FCSTD DOCUMENT  (FreeCAD 0.20R29177 +426 (Git))
Label: ASM_RotationDriver
License: All rights reserved
LicenseURL: http://en.wikipedia.org/wiki/All_rights_reserved
objects: App::Link×8, App::DocumentObjectGroup×3, PartDesign::CoordinateSystem×1, App::FeaturePython×1, App::Part×1
note: 1 computed .brp shape members not serialized (recipe doc carries the construction recipe); baked Part::Feature solids carry a one-line shape summary decoded from their .brp
EXTERNAL_REF file=SerpentinePlate.FCStd obj=LCS_Origin
EXTERNAL_REF file=Stepper17BracketFlat.FCStd obj=LCS_Origin
EXTERNAL_REF file=Stepper17BracketFlat.FCStd obj=Pad
EXTERNAL_REF file=SerpentinePlate.FCStd obj=Assembly
EXTERNAL_REF file=TimingPulleyGT2.FCStd obj=LCS_Origin
EXTERNAL_REF file=TimingPulleyGT2.FCStd obj=Assembly
EXTERNAL_REF file=SerpentinePlate.FCStd obj=LCS_idler1
EXTERNAL_REF file=SmoothIdlerPulleyGT2.FCStd obj=LCS_Origin
EXTERNAL_REF file=SmoothIdlerPulleyGT2.FCStd obj=Assembly
EXTERNAL_REF file=SerpentinePlate.FCStd obj=LCS_idler2
EXTERNAL_REF file=Stepper17BracketFlat.FCStd obj=Assembly
EXTERNAL_REF file=Stepper17.FCStd obj=LCS_mount
EXTERNAL_REF file=Stepper17.FCStd obj=Body
EXTERNAL_REF file=RotationDriverMountingSpacer.FCStd obj=LCS_Origin
EXTERNAL_REF file=Stepper17BracketFlat.FCStd obj=LCS_Mount
EXTERNAL_REF file=RotationDriverMountingSpacer.FCStd obj=Assembly
EXTERNAL_REF file=RotationDriveBelt.FCStd obj=LCS_Origin
EXTERNAL_REF file=RotationDriveBelt.FCStd obj=Assembly

FEATURE [App::DocumentObjectGroup] Parts
FEATURE [PartDesign::CoordinateSystem] LCS_Origin
  AttacherType = Attacher::AttachEngine3D
  MapMode = 2
  Support = -> [X_Axis]
FEATURE [App::FeaturePython] Variables  # WARN: FeaturePython — macro-defined, semantics opaque (R4)
  Type = App::PropertyContainer
FEATURE [App::DocumentObjectGroup] Constraints
FEATURE [App::DocumentObjectGroup] Configurations
FEATURE [App::Link] SerpentinePlate
  AttachedBy = #LCS_Origin
  AttachedTo = Stepper17BracketFlat#LCS_Origin
  AttachmentOffset = pos=(0,0,3) rot=(0,0,1;3.14159rad)
  LinkPlacement = pos=(3e-16,3,0) rot=(1,0,0;4.71239rad)
  LinkedObject = -> <external SerpentinePlate.FCStd>#Assembly
  Placement = pos=(3e-16,3,0) rot=(1,0,0;4.71239rad)
  SolverId = Asm4EE
  expr: .AttachmentOffset.Base.z = <<Stepper17BracketFlat>>#<<Pad>>.Length
  expr: Placement = Stepper17BracketFlat.Placement * Stepper17BracketFlat#LCS_Origin.Placement * AttachmentOffset * SerpentinePlate#LCS_Origin.Placement ^ -1
FEATURE [App::Link] TimingPulleyGT2
  AttachedBy = #LCS_Origin
  AttachedTo = SerpentinePlate#LCS_Origin
  AttachmentOffset = pos=(0,0,23) rot=(0,1,0;3.14159rad)
  LinkPlacement = pos=(2.3e-15,26,0) rot=(0,-0.707107,0.707107;3.14159rad)
  LinkedObject = -> <external TimingPulleyGT2.FCStd>#Assembly
  Placement = pos=(2.3e-15,26,0) rot=(0,-0.707107,0.707107;3.14159rad)
  SolverId = Asm4EE
  expr: Placement = SerpentinePlate.Placement * SerpentinePlate#LCS_Origin.Placement * AttachmentOffset * TimingPulleyGT2#LCS_Origin.Placement ^ -1
FEATURE [App::Link] SmoothIdlerPulleyGT2
  AttachedBy = #LCS_Origin
  AttachedTo = SerpentinePlate#LCS_idler1
  AttachmentOffset = pos=(0,0,1) rot=(0,0,1;0rad)
  LinkPlacement = pos=(16.3,11,7.5) rot=(1,0,0;4.71239rad)
  LinkedObject = -> <external SmoothIdlerPulleyGT2.FCStd>#Assembly
  Placement = pos=(16.3,11,7.5) rot=(1,0,0;4.71239rad)
  SolverId = Asm4EE
  expr: Placement = SerpentinePlate.Placement * SerpentinePlate#LCS_idler1.Placement * AttachmentOffset * SmoothIdlerPulleyGT2#LCS_Origin.Placement ^ -1
FEATURE [App::Link] SmoothIdlerPulleyGT003
  AttachedBy = #LCS_Origin
  AttachedTo = SerpentinePlate#LCS_idler2
  AttachmentOffset = pos=(0,0,1) rot=(0,0,1;0rad)
  LinkPlacement = pos=(-16.3,11,7.5) rot=(1,0,0;4.71239rad)
  LinkedObject = -> <external SmoothIdlerPulleyGT2.FCStd>#Assembly
  Placement = pos=(-16.3,11,7.5) rot=(1,0,0;4.71239rad)
  SolverId = Asm4EE
  expr: Placement = SerpentinePlate.Placement * SerpentinePlate#LCS_idler2.Placement * AttachmentOffset * SmoothIdlerPulleyGT2#LCS_Origin.Placement ^ -1
FEATURE [App::Link] Stepper17BracketFlat
  AttachedBy = #LCS_Origin
  AttachedTo = Parent Assembly#LCS_Origin
  AttachmentOffset = pos=(0,0,0) rot=(0,0.707107,0.707107;3.14159rad)
  LinkPlacement = pos=(0,0,0) rot=(0,0.707107,0.707107;3.14159rad)
  LinkedObject = -> <external Stepper17BracketFlat.FCStd>#Assembly
  Placement = pos=(0,0,0) rot=(0,0.707107,0.707107;3.14159rad)
  SolverId = Asm4EE
  expr: Placement = LCS_Origin.Placement * AttachmentOffset * Stepper17BracketFlat#LCS_Origin.Placement ^ -1
FEATURE [App::Link] Stepper
  AssemblyType = Part::Link
  AttachedBy = #LCS_mount
  AttachedTo = Stepper17BracketFlat#LCS_Origin
  AttachmentOffset = pos=(0,0,0) rot=(0,1,0;3.14159rad)
  LinkPlacement = pos=(0,0,0) rot=(-1,0,0;4.71239rad)
  LinkedObject = -> <external Stepper17.FCStd>#Body
  Placement = pos=(0,0,0) rot=(-1,0,0;4.71239rad)
  SolverId = Asm4EE
  expr: Placement = Stepper17BracketFlat.Placement * Stepper17BracketFlat#LCS_Origin.Placement * AttachmentOffset * Stepper17#LCS_mount.Placement ^ -1
FEATURE [App::Link] RotationDriverMountingSpacer
  AttachedBy = #LCS_Origin
  AttachedTo = Stepper17BracketFlat#LCS_Mount
  AttachmentOffset = pos=(0,0,0) rot=(1,0,0;3.14159rad)
  LinkPlacement = pos=(4.7e-15,0,-53.75) rot=(0,0.707107,-0.707107;3.14159rad)
  LinkedObject = -> <external RotationDriverMountingSpacer.FCStd>#Assembly
  Placement = pos=(4.7e-15,0,-53.75) rot=(0,0.707107,-0.707107;3.14159rad)
  SolverId = Asm4EE
  expr: Placement = Stepper17BracketFlat.Placement * Stepper17BracketFlat#LCS_Mount.Placement * AttachmentOffset * RotationDriverMountingSpacer#LCS_Origin.Placement ^ -1
FEATURE [App::Link] RotationDriveBelt
  AttachedBy = #LCS_Origin
  AttachedTo = TimingPulleyGT2#LCS_Origin
  AttachmentOffset = pos=(0,0,7.7) rot=(0,0,1;3.14159rad)
  LinkPlacement = pos=(2.5e-15,18.3,0) rot=(-1,0,0;4.71239rad)
  LinkedObject = -> <external RotationDriveBelt.FCStd>#Assembly
  Placement = pos=(2.5e-15,18.3,0) rot=(-1,0,0;4.71239rad)
  SolverId = Asm4EE
  expr: Placement = TimingPulleyGT2.Placement * TimingPulleyGT2#LCS_Origin.Placement * AttachmentOffset * RotationDriveBelt#LCS_Origin.Placement ^ -1
FEATURE [App::Part] Assembly
  AssemblyType = Part::Link
  Group = -> [LCS_Origin,Variables,Constraints,Configurations,SerpentinePlate,TimingPulleyGT2,SmoothIdlerPulleyGT2,SmoothIdlerPulleyGT003,Stepper17BracketFlat,Stepper,RotationDriverMountingSpacer,RotationDriveBelt]
  Origin = -> Origin
  Type = Assembly

RESOLVED EXTERNAL PARTS (link-assembly join: the EXTERNAL_REF files above that resolve inside this repo's crawl, each included once):
---- part RotationDriveBelt.FCStd = doc fcstd_e2a3f7d8f1d9 ----
FCSTD DOCUMENT  (FreeCAD 0.20R29177 +426 (Git))
Label: RotationDriveBelt
License: All rights reserved
LicenseURL: http://en.wikipedia.org/wiki/All_rights_reserved
objects: App::DocumentObjectGroup×3, Sketcher::SketchObject×2, PartDesign::Pad×2, PartDesign::Body×2, PartDesign::CoordinateSystem×1, App::FeaturePython×1, App::Part×1
note: 9 computed .brp shape members not serialized (recipe doc carries the construction recipe); baked Part::Feature solids carry a one-line shape summary decoded from their .brp
EXTERNAL_REF file=Params.FCStd obj=Spreadsheet
EXTERNAL_REF file=SerpentinePlate.FCStd obj=Variables

FEATURE [App::DocumentObjectGroup] Parts
FEATURE [PartDesign::CoordinateSystem] LCS_Origin
  AttacherType = Attacher::AttachEngine3D
  MapMode = 2
  Support = -> [X_Axis]
FEATURE [App::FeaturePython] Variables  # WARN: FeaturePython — macro-defined, semantics opaque (R4)
  Type = App::PropertyContainer
FEATURE [App::DocumentObjectGroup] Constraints
FEATURE [App::DocumentObjectGroup] Configurations
FEATURE [Sketcher::SketchObject] Sketch
  FullyConstrained = true
  MapMode = 5
  Support = -> [XY_Plane001]
  expr: Constraints[0] = <<SerpentinePlate>>#<<Variables>>.IdlerMountOffsetX
  expr: Constraints[10] = <<Params>>#<<Params>>.CeilingPlateDiameter / 2 + <<Params>>#<<Params>>.RotationDriveOffset
  expr: Constraints[11] = <<SerpentinePlate>>#<<Variables>>.IdlerMountOffsetY
  expr: Constraints[3] = <<Params>>#<<Params>>.CeilingPlateDiameter + 1
  sketch-geometry (9):
    g0: ArcOfCircle CenterX=1.16e-14 CenterY=-260.5 CenterZ=0 NormalX=0 NormalY=0 NormalZ=1 AngleXU=0 Radius=232 StartAngle=2.20872 EndAngle=7.21605
    g1: ArcOfCircle CenterX=16.3 CenterY=7.5 CenterZ=0 NormalX=0 NormalY=0 NormalZ=1 AngleXU=0 Radius=7 StartAngle=0.932868 EndAngle=2.93081
    g2: ArcOfCircle CenterX=0 CenterY=0 CenterZ=0 NormalX=0 NormalY=0 NormalZ=1 AngleXU=0 Radius=7.37 StartAngle=3.35238 EndAngle=6.0724
    g3: ArcOfCircle CenterX=1.16e-14 CenterY=-260.5 CenterZ=0 NormalX=0 NormalY=0 NormalZ=1 AngleXU=0 Radius=232 StartAngle=0.932868 EndAngle=1.5708
    g4: ArcOfCircle CenterX=-16.3 CenterY=7.5 CenterZ=0 NormalX=0 NormalY=0 NormalZ=1 AngleXU=0 Radius=7 StartAngle=0.210787 EndAngle=2.20872
    g5: LineSegment StartX=7.20688 StartY=-1.54202 StartZ=0 EndX=9.45493 EndY=8.96461 EndZ=0
    g6: LineSegment StartX=138.163 StartY=-74.1271 StartZ=0 EndX=20.4687 EndY=13.1233 EndZ=0
    g7: LineSegment StartX=-7.20688 StartY=-1.54202 StartZ=0 EndX=-9.45493 EndY=8.96461 EndZ=0
    g8: LineSegment StartX=-138.163 StartY=-74.1271 StartZ=0 EndX=-20.4687 EndY=13.1233 EndZ=0
  constraints (22):
    c: DistanceX(g2,g1) = 16.3
    c: Radius(g1) = 7
    c: Radius(g2) = 7.37
    c: Diameter(g0) = 464
    c: PointOnObject(g3,g-2)
    c: Tangent(g3,g0) = -1.5708
    c: Coincident(g3,g0)
    c: Coincident(g2,g-1)
    c: PointOnObject(g0,g-2)
    c: Equal(g4,g1)
    c: DistanceY(g0,g2) = 260.5
    c: DistanceY(g2,g1) = 7.5
    c: Tangent(g5,g1) = 1.5708
    c: Tangent(g5,g2) = -1.5708
    c: Tangent(g6,g1) = -1.5708
    c: Tangent(g6,g0) = -1.5708
    c: Tangent(g7,g4) = -1.5708
    c: Tangent(g7,g2) = 1.5708
    c: Tangent(g8,g4) = 1.5708
    c: Tangent(g8,g0) = 1.5708
    c: Equal(g7,g5)
    c: Equal(g6,g8)
FEATURE [PartDesign::Pad] Pad
  Direction = (0,0,1)
  Length = 6
  Length2 = 10
  Profile = -> Sketch
  ReferenceAxis = -> Sketch [N_Axis]
  Type = 0
FEATURE [PartDesign::Body] Body  label="PerimeterCalc"
  Group = -> [Sketch,Pad]
  Origin = -> Origin001
  Tip = -> Pad
FEATURE [Sketcher::SketchObject] Sketch001
  FullyConstrained = true
  MapMode = 5
  Support = -> [XY_Plane002]
  expr: Constraints[0] = <<SerpentinePlate>>#<<Variables>>.IdlerMountOffsetX
  expr: Constraints[10] = <<Params>>#<<Params>>.CeilingPlateDiameter / 2 + <<Params>>#<<Params>>.RotationDriveOffset
  expr: Constraints[11] = <<SerpentinePlate>>#<<Variables>>.IdlerMountOffsetY
  expr: Constraints[3] = <<Params>>#<<Params>>.CeilingPlateDiameter + 1
  sketch-geometry (19):
    g0: ArcOfCircle CenterX=0 CenterY=-260.5 CenterZ=0 NormalX=0 NormalY=0 NormalZ=1 AngleXU=0 Radius=232 StartAngle=2.20872 EndAngle=7.21605
    g1: ArcOfCircle CenterX=16.3 CenterY=7.5 CenterZ=0 NormalX=0 NormalY=0 NormalZ=1 AngleXU=0 Radius=7 StartAngle=0.932868 EndAngle=2.93081
    g2: ArcOfCircle CenterX=0 CenterY=0 CenterZ=0 NormalX=0 NormalY=0 NormalZ=1 AngleXU=0 Radius=7.37 StartAngle=3.35238 EndAngle=6.0724
    g3: ArcOfCircle CenterX=0 CenterY=-260.5 CenterZ=0 NormalX=0 NormalY=0 NormalZ=1 AngleXU=0 Radius=232 StartAngle=0.932868 EndAngle=1.5708
    g4: ArcOfCircle CenterX=-16.3 CenterY=7.5 CenterZ=0 NormalX=0 NormalY=0 NormalZ=1 AngleXU=0 Radius=7 StartAngle=0.210787 EndAngle=2.20872
    g5: LineSegment StartX=7.20688 StartY=-1.54202 StartZ=0 EndX=9.45493 EndY=8.96461 EndZ=0
    g6: LineSegment StartX=138.163 StartY=-74.1271 StartZ=0 EndX=20.4687 EndY=13.1233 EndZ=0
    g7: LineSegment StartX=-7.20688 StartY=-1.54202 StartZ=0 EndX=-9.45493 EndY=8.96461 EndZ=0
    g8: LineSegment StartX=-138.163 StartY=-74.1271 StartZ=0 EndX=-20.4687 EndY=13.1233 EndZ=0
    g9: ArcOfCircle CenterX=0 CenterY=-260.5 CenterZ=0 NormalX=0 NormalY=0 NormalZ=1 AngleXU=0 Radius=230 StartAngle=2.20872 EndAngle=7.21605
    g10: ArcOfCircle CenterX=16.3 CenterY=7.5 CenterZ=0 NormalX=0 NormalY=0 NormalZ=1 AngleXU=0 Radius=5 StartAngle=0.932868 EndAngle=2.93081
    g11: ArcOfCircle CenterX=0 CenterY=0 CenterZ=0 NormalX=0 NormalY=0 NormalZ=1 AngleXU=0 Radius=9.37 StartAngle=3.35238 EndAngle=6.0724
    g12: ArcOfCircle CenterX=-16.3 CenterY=7.5 CenterZ=0 NormalX=0 NormalY=0 NormalZ=1 AngleXU=0 Radius=5 StartAngle=0.210787 EndAngle=2.20872
    g13: LineSegment StartX=9.16261 StartY=-1.96048 StartZ=0 EndX=11.4107 EndY=8.54615 EndZ=0
    g14: LineSegment StartX=136.972 StartY=-75.7338 StartZ=0 EndX=19.2777 EndY=11.5167 EndZ=0
    g15: LineSegment StartX=-9.16261 StartY=-1.96048 StartZ=0 EndX=-11.4107 EndY=8.54615 EndZ=0
    g16: LineSegment StartX=-136.972 StartY=-75.7338 StartZ=0 EndX=-19.2777 EndY=11.5167 EndZ=0
    g17: LineSegment StartX=11.4107 StartY=8.54615 StartZ=0 EndX=9.45493 EndY=8.96461 EndZ=0
    g18: LineSegment StartX=138.163 StartY=-74.1271 StartZ=0 EndX=136.972 EndY=-75.7338 EndZ=0
  constraints (45):
    c: DistanceX(g2,g1) = 16.3
    c: Radius(g1) = 7
    c: Radius(g2) = 7.37
    c: Diameter(g0) = 464
    c: PointOnObject(g3,g-2)
    c: Tangent(g3,g0) = -1.5708
    c: Coincident(g3,g0)
    c: Coincident(g2,g-1)
    c: PointOnObject(g0,g-2)
    c: Equal(g4,g1)
    c: DistanceY(g0,g2) = 260.5
    c: DistanceY(g2,g1) = 7.5
    c: Tangent(g5,g1) = 1.5708
    c: Tangent(g5,g2) = -1.5708
    c: Tangent(g6,g1) = -1.5708
    c: Tangent(g6,g0) = -1.5708
    c: Tangent(g7,g4) = -1.5708
    c: Tangent(g7,g2) = 1.5708
    c: Tangent(g8,g4) = 1.5708
    c: Tangent(g8,g0) = 1.5708
    c: Equal(g7,g5)
    c: Equal(g6,g8)
    c: DistanceX(g11,g10) = 16.3
    c: DistanceY(g11,g10) = 7.5
    c: Tangent(g13,g10) = 1.5708
    c: Tangent(g13,g11) = -1.5708
    c: Tangent(g14,g10) = -1.5708
    c: Tangent(g14,g9) = -1.5708
    c: Tangent(g15,g12) = -1.5708
    c: Tangent(g15,g11) = 1.5708
    c: Tangent(g16,g12) = 1.5708
    c: Tangent(g16,g9) = 1.5708
    c: Equal(g15,g13)
    c: Coincident(g9,g0)
    c: Coincident(g11,g2)
    c: Coincident(g12,g4)
    c: Coincident(g17,g10)
    c: Perpendicular(g13,g17)
    c: PointOnObject(g17,g5)
    c: Parallel(g13,g5)
    c: Distance(g17) = 2
    c: Coincident(g18,g0)
    c: Perpendicular(g6,g18)
    c: PointOnObject(g18,g14)
    c: Equal(g18,g17)
FEATURE [PartDesign::Pad] Pad001
  Direction = (0,0,1)
  Length = 6
  Length2 = 10
  Profile = -> Sketch001
  ReferenceAxis = -> Sketch001 [N_Axis]
  Type = 0
FEATURE [PartDesign::Body] Body001
  Group = -> [Sketch001,Pad001]
  Origin = -> Origin002
  Tip = -> Pad001
FEATURE [App::Part] Assembly
  AssemblyType = Part::Link
  Group = -> [LCS_Origin,Variables,Constraints,Configurations,Body,Body001]
  Origin = -> Origin
  Type = Assembly
---- part RotationDriverMountingSpacer.FCStd = doc fcstd_c8136d02d082 ----
FCSTD DOCUMENT  (FreeCAD 0.20R29177 +426 (Git))
Label: RotationDriverMountingSpacer
License: All rights reserved
LicenseURL: http://en.wikipedia.org/wiki/All_rights_reserved
objects: Part::FeaturePython×16, App::DocumentObjectGroup×8, Sketcher::SketchObject×2, PartDesign::CoordinateSystem×1, App::FeaturePython×1, PartDesign::Pad×1, PartDesign::Hole×1, PartDesign::Body×1, App::Part×1
note: 24 computed .brp shape members not serialized (recipe doc carries the construction recipe); baked Part::Feature solids carry a one-line shape summary decoded from their .brp
EXTERNAL_REF file=Params.FCStd obj=Spreadsheet
EXTERNAL_REF file=Stepper17BracketFlat.FCStd obj=Pad

FEATURE [App::DocumentObjectGroup] Parts
FEATURE [PartDesign::CoordinateSystem] LCS_Origin
  AttacherType = Attacher::AttachEngine3D
  MapMode = 2
  Support = -> [X_Axis]
FEATURE [App::FeaturePython] Variables  # WARN: FeaturePython — macro-defined, semantics opaque (R4)
  BracketHoleSpacing = 30
  Type = App::PropertyContainer
FEATURE [App::DocumentObjectGroup] Constraints
FEATURE [App::DocumentObjectGroup] Configurations
FEATURE [Sketcher::SketchObject] Sketch
  FullyConstrained = true
  MapMode = 5
  Support = -> [XY_Plane001]
  expr: Constraints[26] = <<Variables>>.BracketHoleSpacing
  sketch-geometry (24):
    g0: LineSegment StartX=-15 StartY=-15 StartZ=0 EndX=-15 EndY=15 EndZ=0
    g1: LineSegment StartX=-15 StartY=15 StartZ=0 EndX=15 EndY=15 EndZ=0
    g2: LineSegment StartX=15 StartY=15 StartZ=0 EndX=15 EndY=-15 EndZ=0
    g3: LineSegment StartX=15 StartY=-15 StartZ=0 EndX=-15 EndY=-15 EndZ=0
    g4: GeomPoint X=0 Y=0 Z=0
    g5: ArcOfCircle CenterX=15 CenterY=15 CenterZ=0 NormalX=0 NormalY=0 NormalZ=1 AngleXU=0 Radius=2.15 StartAngle=0 EndAngle=3.14159
    g6: ArcOfCircle CenterX=15 CenterY=-15 CenterZ=0 NormalX=0 NormalY=0 NormalZ=1 AngleXU=0 Radius=2.15 StartAngle=3.14159 EndAngle=6.28319
    g7: LineSegment StartX=12.85 StartY=15 StartZ=0 EndX=12.85 EndY=-15 EndZ=0
    g8: LineSegment StartX=17.15 StartY=-15 StartZ=0 EndX=17.15 EndY=15 EndZ=0
    g9: ArcOfCircle CenterX=-15 CenterY=15 CenterZ=0 NormalX=0 NormalY=0 NormalZ=1 AngleXU=0 Radius=2.15 StartAngle=0 EndAngle=3.14159
    g10: ArcOfCircle CenterX=-15 CenterY=-15 CenterZ=0 NormalX=0 NormalY=0 NormalZ=1 AngleXU=0 Radius=2.15 StartAngle=3.14159 EndAngle=6.28319
    g11: LineSegment StartX=-17.15 StartY=15 StartZ=0 EndX=-17.15 EndY=-15 EndZ=0
    g12: LineSegment StartX=-12.85 StartY=-15 StartZ=0 EndX=-12.85 EndY=15 EndZ=0
    g13: ArcOfCircle CenterX=-15 CenterY=15 CenterZ=0 NormalX=0 NormalY=0 NormalZ=1 AngleXU=0 Radius=10 StartAngle=1.5708 EndAngle=3.14159
    g14: LineSegment StartX=-15 StartY=25 StartZ=0 EndX=15 EndY=25 EndZ=0
    g15: ArcOfCircle CenterX=15 CenterY=15 CenterZ=0 NormalX=0 NormalY=0 NormalZ=1 AngleXU=0 Radius=10 StartAngle=1e-16 EndAngle=1.5708
    g16: LineSegment StartX=25 StartY=15 StartZ=0 EndX=25 EndY=-15 EndZ=0
    g17: ArcOfCircle CenterX=15 CenterY=-15 CenterZ=0 NormalX=0 NormalY=0 NormalZ=1 AngleXU=0 Radius=10 StartAngle=4.71239 EndAngle=6.28319
    g18: LineSegment StartX=15 StartY=-25 StartZ=0 EndX=-15 EndY=-25 EndZ=0
    g19: ArcOfCircle CenterX=-15 CenterY=-15 CenterZ=0 NormalX=0 NormalY=0 NormalZ=1 AngleXU=0 Radius=10 StartAngle=3.14159 EndAngle=4.71239
    g20: LineSegment StartX=-25 StartY=-15 StartZ=0 EndX=-25 EndY=15 EndZ=0
    g21: GeomPoint X=-25 Y=25 Z=0
    g22: GeomPoint X=25 Y=-25 Z=0
    g23: Circle CenterX=0 CenterY=0 CenterZ=0 NormalX=0 NormalY=0 NormalZ=1 AngleXU=0 Radius=14
  constraints (52):
    c: Coincident(g0,g1)
    c: Coincident(g1,g2)
    c: Coincident(g2,g3)
    c: Coincident(g3,g0)
    c: Horizontal(g1)
    c: Horizontal(g3)
    c: Vertical(g0)
    c: Vertical(g2)
    c: Symmetric(g1,g0,g4)
    c: Coincident(g4,g-1)
    c: Tangent(g5,g7) = -1.5708
    c: Tangent(g7,g6) = -1.5708
    c: Tangent(g6,g8) = -1.5708
    c: Tangent(g8,g5) = -1.5708
    c: Equal(g5,g6)
    c: Coincident(g5,g1)
    c: Coincident(g6,g2)
    c: Tangent(g9,g11) = -1.5708
    c: Tangent(g11,g10) = -1.5708
    c: Tangent(g10,g12) = -1.5708
    c: Tangent(g12,g9) = -1.5708
    c: Equal(g9,g10)
    c: Coincident(g9,g0)
    c: Coincident(g10,g0)
    c: Equal(g5,g9)
    c: Diameter(g5) = 4.3
    c: DistanceX(g1,g1) = 30
    c: Equal(g2,g1)
    c: Tangent(g13,g14) = 1.5708
    c: Tangent(g14,g15) = 1.5708
    c: Tangent(g15,g16) = 1.5708
    c: Tangent(g16,g17) = 1.5708
    c: Tangent(g17,g18) = 1.5708
    c: Tangent(g18,g19) = 1.5708
    c: Tangent(g19,g20) = 1.5708
    c: Tangent(g20,g13) = 1.5708
    c: Horizontal(g14)
    c: Horizontal(g18)
    c: Vertical(g16)
    c: Vertical(g20)
    c: Equal(g13,g15)
    c: Equal(g15,g17)
    c: Equal(g17,g19)
    c: PointOnObject(g21,g14)
    c: PointOnObject(g21,g20)
    c: PointOnObject(g22,g16)
    c: PointOnObject(g22,g18)
    c: Coincident(g13,g9)
    c: Coincident(g17,g6)
    c: DistanceX(g13,g15) = 50
    c: Coincident(g23,g4)
    c: Diameter(g23) = 28
FEATURE [PartDesign::Pad] Pad
  Direction = (0,0,1)
  Length = 9
  Length2 = 10
  Profile = -> Sketch
  ReferenceAxis = -> Sketch [N_Axis]
  Type = 0
FEATURE [Sketcher::SketchObject] Sketch001
  FullyConstrained = true
  MapMode = 5
  Support = -> [XY_Plane001]
  sketch-geometry (9):
    g0: LineSegment StartX=-15 StartY=-15 StartZ=0 EndX=-15 EndY=15 EndZ=0
    g1: LineSegment StartX=-15 StartY=15 StartZ=0 EndX=15 EndY=15 EndZ=0
    g2: LineSegment StartX=15 StartY=15 StartZ=0 EndX=15 EndY=-15 EndZ=0
    g3: LineSegment StartX=15 StartY=-15 StartZ=0 EndX=-15 EndY=-15 EndZ=0
    g4: GeomPoint X=0 Y=0 Z=0
    g5: Circle CenterX=15 CenterY=15 CenterZ=0 NormalX=0 NormalY=0 NormalZ=1 AngleXU=0 Radius=1
    g6: Circle CenterX=15 CenterY=-15 CenterZ=0 NormalX=0 NormalY=0 NormalZ=1 AngleXU=0 Radius=1
    g7: Circle CenterX=-15 CenterY=15 CenterZ=0 NormalX=0 NormalY=0 NormalZ=1 AngleXU=0 Radius=1
    g8: Circle CenterX=-15 CenterY=-15 CenterZ=0 NormalX=0 NormalY=0 NormalZ=1 AngleXU=0 Radius=1
  constraints (20):
    c: Coincident(g0,g1)
    c: Coincident(g1,g2)
    c: Coincident(g2,g3)
    c: Coincident(g3,g0)
    c: Horizontal(g1)
    c: Horizontal(g3)
    c: Vertical(g0)
    c: Vertical(g2)
    c: Symmetric(g1,g0,g4)
    c: Coincident(g4,g-1)
    c: DistanceX(g1,g1) = 30
    c: Equal(g2,g1)
    c: Coincident(g5,g1)
    c: Coincident(g6,g2)
    c: Coincident(g7,g0)
    c: Coincident(g8,g0)
    c: Equal(g8,g6)
    c: Equal(g6,g5)
    c: Equal(g5,g7)
    c: Diameter(g5) = 2
FEATURE [PartDesign::Hole] Hole  label="BracketMountHoles"
  BaseFeature = -> Pad
  CustomThreadClearance = 0
  Depth = 143.988
  DepthType = 1
  Diameter = 4.8
  DrillForDepth = false
  DrillPoint = 1
  DrillPointAngle = 118
  HoleCutCountersinkAngle = 90
  HoleCutCustomValues = false
  HoleCutDepth = 0
  HoleCutDiameter = 6.1
  HoleCutType = 0
  ModelThread = false
  Profile = -> Sketch001
  Reversed = true
  Tapered = false
  TaperedAngle = 90
  ThreadClass = 0
  ThreadDepth = 143.988
  ThreadDepthType = 0
  ThreadDirection = 0
  ThreadFit = 2
  ThreadSize = 0
  ThreadType = 0
  Threaded = false
  UseCustomThreadClearance = false
FEATURE [PartDesign::Body] Body
  Group = -> [Sketch,Pad,Sketch001,Hole]
  Origin = -> Origin001
  Tip = -> Hole
FEATURE [Part::FeaturePython] Washer  label="M4-Washer"  # Fasteners workbench fastener (typed FeaturePython)
  Placement = pos=(15,-15,11.656) rot=(0,0,1;0rad)
  baseObject = -> Sketch001 [Edge2]
  diameter = 5
  invert = false
  matchOuter = true
  offset = 11.656
  type = 3
  expr: offset = <<Pad>>.Length + <<Params>>#<<Params>>.SheetMetalThickness * 1mm
FEATURE [Part::FeaturePython] Screw  label="M4x20-Screw"  # Fasteners workbench fastener (typed FeaturePython)
  Placement = pos=(15,-15,12.456) rot=(0,0,1;0rad)
  baseObject = -> Washer [Edge1]
  diameter = 5
  invert = false
  leftHanded = false
  length = 6
  lengthCustom = 20
  matchOuter = true
  offset = 0
  thread = false
  type = 34
FEATURE [Part::FeaturePython] Washer001  label="M4-Washer022"  # Fasteners workbench fastener (typed FeaturePython)
  Placement = pos=(15,-15,-3) rot=(1,0,0;3.14159rad)
  baseObject = -> Washer [Edge3]
  diameter = 5
  invert = true
  matchOuter = true
  offset = 14.656
  type = 3
  expr: offset = <<Pad>>.Length + <<Params>>#<<Params>>.SheetMetalThickness * 1mm + <<Stepper17BracketFlat>>#<<Pad>>.Length
FEATURE [Part::FeaturePython] Nut  label="M4-Nut"  # Fasteners workbench fastener (typed FeaturePython)
  Placement = pos=(15,-15,-3.8) rot=(1,0,0;3.14159rad)
  baseObject = -> Washer001 [Edge1]
  diameter = 6
  invert = false
  leftHanded = false
  matchOuter = true
  offset = 0
  thread = false
  type = 7
FEATURE [App::DocumentObjectGroup] Hole1
  Group = -> [Screw,Washer,Washer001,Nut]
FEATURE [Part::FeaturePython] Nut001  label="M4-Nut010"  # Fasteners workbench fastener (typed FeaturePython)
  Placement = pos=(-15,-15,-3.8) rot=(1,0,0;3.14159rad)
  baseObject = -> Washer003 [Edge1]
  diameter = 6
  invert = false
  leftHanded = false
  matchOuter = true
  offset = 0
  thread = false
  type = 7
FEATURE [Part::FeaturePython] Screw001  label="M4x20-Screw010"  # Fasteners workbench fastener (typed FeaturePython)
  Placement = pos=(-15,-15,12.456) rot=(0,0,1;0rad)
  baseObject = -> Washer002 [Edge1]
  diameter = 5
  invert = false
  leftHanded = false
  length = 6
  lengthCustom = 20
  matchOuter = true
  offset = 0
  thread = false
  type = 34
FEATURE [Part::FeaturePython] Washer002  label="M4-Washer023"  # Fasteners workbench fastener (typed FeaturePython)
  Placement = pos=(-15,-15,11.656) rot=(0,0,1;0rad)
  baseObject = -> Sketch001 [Edge4]
  diameter = 5
  invert = false
  matchOuter = true
  offset = 11.656
  type = 3
  expr: offset = <<Pad>>.Length + <<Params>>#<<Params>>.SheetMetalThickness * 1mm
FEATURE [Part::FeaturePython] Washer003  label="M4-Washer024"  # Fasteners workbench fastener (typed FeaturePython)
  Placement = pos=(-15,-15,-3) rot=(1,0,0;3.14159rad)
  baseObject = -> Washer002 [Edge3]
  diameter = 5
  invert = true
  matchOuter = true
  offset = 14.656
  type = 3
  expr: offset = <<Pad>>.Length + <<Params>>#<<Params>>.SheetMetalThickness * 1mm + <<Stepper17BracketFlat>>#<<Pad>>.Length
FEATURE [App::DocumentObjectGroup] Hole002
  Group = -> [Screw001,Washer002,Washer003,Nut001]
FEATURE [Part::FeaturePython] Nut002  label="M4-Nut011"  # Fasteners workbench fastener (typed FeaturePython)
  Placement = pos=(-15,15,-3.8) rot=(1,0,0;3.14159rad)
  baseObject = -> Washer005 [Edge1]
  diameter = 6
  invert = false
  leftHanded = false
  matchOuter = true
  offset = 0
  thread = false
  type = 7
FEATURE [Part::FeaturePython] Screw002  label="M4x20-Screw011"  # Fasteners workbench fastener (typed FeaturePython)
  Placement = pos=(-15,15,12.456) rot=(0,0,1;0rad)
  baseObject = -> Washer004 [Edge1]
  diameter = 5
  invert = false
  leftHanded = false
  length = 6
  lengthCustom = 20
  matchOuter = true
  offset = 0
  thread = false
  type = 34
FEATURE [Part::FeaturePython] Washer004  label="M4-Washer025"  # Fasteners workbench fastener (typed FeaturePython)
  Placement = pos=(-15,15,11.656) rot=(0,0,1;0rad)
  baseObject = -> Sketch001 [Edge3]
  diameter = 5
  invert = false
  matchOuter = true
  offset = 11.656
  type = 3
  expr: offset = <<Pad>>.Length + <<Params>>#<<Params>>.SheetMetalThickness * 1mm
FEATURE [Part::FeaturePython] Washer005  label="M4-Washer026"  # Fasteners workbench fastener (typed FeaturePython)
  Placement = pos=(-15,15,-3) rot=(1,0,0;3.14159rad)
  baseObject = -> Washer004 [Edge3]
  diameter = 5
  invert = true
  matchOuter = true
  offset = 14.656
  type = 3
  expr: offset = <<Pad>>.Length + <<Params>>#<<Params>>.SheetMetalThickness * 1mm + <<Stepper17BracketFlat>>#<<Pad>>.Length
FEATURE [App::DocumentObjectGroup] Hole003
  Group = -> [Screw002,Washer004,Washer005,Nut002]
FEATURE [Part::FeaturePython] Nut003  label="M4-Nut012"  # Fasteners workbench fastener (typed FeaturePython)
  Placement = pos=(15,15,-3.8) rot=(1,0,0;3.14159rad)
  baseObject = -> Washer007 [Edge1]
  diameter = 6
  invert = false
  leftHanded = false
  matchOuter = true
  offset = 0
  thread = false
  type = 7
FEATURE [Part::FeaturePython] Screw003  label="M4x20-Screw012"  # Fasteners workbench fastener (typed FeaturePython)
  Placement = pos=(15,15,12.456) rot=(0,0,1;0rad)
  baseObject = -> Washer006 [Edge1]
  diameter = 5
  invert = false
  leftHanded = false
  length = 6
  lengthCustom = 20
  matchOuter = true
  offset = 0
  thread = false
  type = 34
FEATURE [Part::FeaturePython] Washer006  label="M4-Washer027"  # Fasteners workbench fastener (typed FeaturePython)
  Placement = pos=(15,15,11.656) rot=(0,0,1;0rad)
  baseObject = -> Sketch001 [Edge1]
  diameter = 5
  invert = false
  matchOuter = true
  offset = 11.656
  type = 3
  expr: offset = <<Pad>>.Length + <<Params>>#<<Params>>.SheetMetalThickness * 1mm
FEATURE [Part::FeaturePython] Washer007  label="M4-Washer028"  # Fasteners workbench fastener (typed FeaturePython)
  Placement = pos=(15,15,-3) rot=(1,0,0;3.14159rad)
  baseObject = -> Washer006 [Edge3]
  diameter = 5
  invert = true
  matchOuter = true
  offset = 14.656
  type = 3
  expr: offset = <<Pad>>.Length + <<Params>>#<<Params>>.SheetMetalThickness * 1mm + <<Stepper17BracketFlat>>#<<Pad>>.Length
FEATURE [App::DocumentObjectGroup] Hole004
  Group = -> [Screw003,Washer006,Washer007,Nut003]
FEATURE [App::DocumentObjectGroup] Fasteners
  Group = -> [Hole1,Hole002,Hole003,Hole004]
FEATURE [App::Part] Assembly
  AssemblyType = Part::Link
  Group = -> [LCS_Origin,Variables,Constraints,Configurations,Body,Fasteners,Washer,Screw,Washer001,Nut,Hole1,Washer002,Screw001,Washer003,Nut001,Hole002,Washer005,Nut002,Screw002,Washer004,Hole003,Washer007,Screw003,Nut003,Washer006,Hole004]
  Origin = -> Origin
  Type = Assembly
---- part SerpentinePlate.FCStd = doc fcstd_52ecc4b848b1 ----
FCSTD DOCUMENT  (FreeCAD 0.20R29177 +426 (Git))
Label: SerpentinePlate
License: All rights reserved
LicenseURL: http://en.wikipedia.org/wiki/All_rights_reserved
objects: Part::FeaturePython×8, App::DocumentObjectGroup×4, PartDesign::Hole×4, PartDesign::CoordinateSystem×3, Sketcher::SketchObject×3, App::FeaturePython×1, PartDesign::Pad×1, PartDesign::Body×1, App::Part×1
note: 25 computed .brp shape members not serialized (recipe doc carries the construction recipe); baked Part::Feature solids carry a one-line shape summary decoded from their .brp

FEATURE [App::DocumentObjectGroup] Parts
FEATURE [PartDesign::CoordinateSystem] LCS_Origin
  AttacherType = Attacher::AttachEngine3D
  MapMode = 2
  Support = -> [X_Axis]
FEATURE [App::FeaturePython] Variables  # WARN: FeaturePython — macro-defined, semantics opaque (R4)
  IdlerMountOffsetX = 16.3
  IdlerMountOffsetY = 7.5
  Type = App::PropertyContainer
FEATURE [App::DocumentObjectGroup] Constraints
FEATURE [App::DocumentObjectGroup] Configurations
FEATURE [Sketcher::SketchObject] Sketch
  FullyConstrained = true
  MapMode = 5
  Support = -> [XY_Plane001]
  sketch-geometry (23):
    g0: LineSegment StartX=-15.5 StartY=15.5 StartZ=0 EndX=-15.5 EndY=-15.5 EndZ=0
    g1: LineSegment StartX=-15.5 StartY=-15.5 StartZ=0 EndX=15.5 EndY=-15.5 EndZ=0
    g2: LineSegment StartX=15.5 StartY=-15.5 StartZ=0 EndX=15.5 EndY=15.5 EndZ=0
    g3: LineSegment StartX=15.5 StartY=15.5 StartZ=0 EndX=-15.5 EndY=15.5 EndZ=0
    g4: GeomPoint X=0 Y=0 Z=0
    g5: Circle CenterX=-15.5 CenterY=15.5 CenterZ=0 NormalX=0 NormalY=0 NormalZ=1 AngleXU=0 Radius=1.7
    g6: Circle CenterX=15.5 CenterY=15.5 CenterZ=0 NormalX=0 NormalY=0 NormalZ=1 AngleXU=0 Radius=1.7
    g7: Circle CenterX=15.5 CenterY=-15.5 CenterZ=0 NormalX=0 NormalY=0 NormalZ=1 AngleXU=0 Radius=1.7
    g8: Circle CenterX=-15.5 CenterY=-15.5 CenterZ=0 NormalX=0 NormalY=0 NormalZ=1 AngleXU=0 Radius=1.7
    g9: Circle CenterX=0 CenterY=0 CenterZ=0 NormalX=0 NormalY=0 NormalZ=1 AngleXU=0 Radius=11.3
    g10: Circle CenterX=0 CenterY=0 CenterZ=0 NormalX=0 NormalY=0 NormalZ=1 AngleXU=0 Radius=6.11
    g11: ArcOfCircle CenterX=-15.5 CenterY=13 CenterZ=0 NormalX=0 NormalY=0 NormalZ=1 AngleXU=0 Radius=7.5 StartAngle=1.5708 EndAngle=3.14159
    g12: LineSegment StartX=-15.5 StartY=20.5 StartZ=0 EndX=15.5 EndY=20.5 EndZ=0
    g13: ArcOfCircle CenterX=15.5 CenterY=13 CenterZ=0 NormalX=0 NormalY=0 NormalZ=1 AngleXU=0 Radius=7.5 StartAngle=1e-16 EndAngle=1.5708
    g14: LineSegment StartX=23 StartY=13 StartZ=0 EndX=23 EndY=-13 EndZ=0
    g15: ArcOfCircle CenterX=15.5 CenterY=-13 CenterZ=0 NormalX=0 NormalY=0 NormalZ=1 AngleXU=0 Radius=7.5 StartAngle=4.71239 EndAngle=6.28319
    g16: LineSegment StartX=15.5 StartY=-20.5 StartZ=0 EndX=-15.5 EndY=-20.5 EndZ=0
    g17: ArcOfCircle CenterX=-15.5 CenterY=-13 CenterZ=0 NormalX=0 NormalY=0 NormalZ=1 AngleXU=0 Radius=7.5 StartAngle=3.14159 EndAngle=4.71239
    g18: LineSegment StartX=-23 StartY=-13 StartZ=0 EndX=-23 EndY=13 EndZ=0
    g19: GeomPoint X=-23 Y=20.5 Z=0
    g20: GeomPoint X=23 Y=-20.5 Z=0
    g21: LineSegment StartX=-15.5 StartY=20.5 StartZ=0 EndX=-15.5 EndY=15.5 EndZ=0
    g22: LineSegment StartX=15.5 StartY=-20.5 StartZ=0 EndX=15.5 EndY=-15.5 EndZ=0
  constraints (52):
    c: Coincident(g0,g1)
    c: Coincident(g1,g2)
    c: Coincident(g2,g3)
    c: Coincident(g3,g0)
    c: Horizontal(g1)
    c: Horizontal(g3)
    c: Vertical(g0)
    c: Vertical(g2)
    c: Symmetric(g1,g0,g4)
    c: Coincident(g4,g-1)
    c: Coincident(g5,g0)
    c: Coincident(g6,g2)
    c: Coincident(g7,g1)
    c: Coincident(g8,g0)
    c: Equal(g3,g0)
    c: Equal(g6,g5)
    c: Equal(g5,g8)
    c: Equal(g8,g7)
    c: Diameter(g6) = 3.4
    c: Coincident(g9,g4)
    c: Diameter(g9) = 22.6
    c: Coincident(g10,g9)
    c: Diameter(g10) = 12.22
    c: DistanceX(g3,g3) = 31
    c: Tangent(g11,g12) = 1.5708
    c: Tangent(g12,g13) = 1.5708
    c: Tangent(g13,g14) = 1.5708
    c: Tangent(g14,g15) = 1.5708
    c: Tangent(g15,g16) = 1.5708
    c: Tangent(g16,g17) = 1.5708
    c: Tangent(g17,g18) = 1.5708
    c: Tangent(g18,g11) = 1.5708
    c: Horizontal(g12)
    c: Horizontal(g16)
    c: Vertical(g14)
    c: Vertical(g18)
    c: Equal(g11,g13)
    c: Equal(g13,g15)
    c: Equal(g15,g17)
    c: PointOnObject(g19,g12)
    c: PointOnObject(g19,g18)
    c: PointOnObject(g20,g14)
    c: PointOnObject(g20,g16)
    c: DistanceX(g11,g13) = 46
    c: PointOnObject(g15,g2)
    c: DistanceY(g15,g7) = 5
    c: PointOnObject(g11,g0)
    c: Coincident(g21,g11)
    c: Coincident(g21,g0)
    c: Coincident(g22,g15)
    c: Coincident(g22,g1)
    c: Equal(g22,g21)
FEATURE [Sketcher::SketchObject] Sketch001
  AttachmentOffset = pos=(16.3,-7.5,0.5) rot=(0,0,1;0rad)
  FullyConstrained = true
  MapMode = 5
  Placement = pos=(16.3,-7.5,0.5) rot=(0,0,1;0rad)
  Support = -> [XY_Plane001]
  expr: .AttachmentOffset.Base.x = <<Variables>>.IdlerMountOffsetX
  expr: .AttachmentOffset.Base.y = <<Variables>>.IdlerMountOffsetY * -1
  expr: Constraints[5] = <<Variables>>.IdlerMountOffsetX * 2
  sketch-geometry (3):
    g0: GeomPoint X=0 Y=0 Z=0
    g1: Circle CenterX=0 CenterY=0 CenterZ=0 NormalX=0 NormalY=0 NormalZ=1 AngleXU=0 Radius=2.5
    g2: Circle CenterX=-32.6 CenterY=0 CenterZ=0 NormalX=0 NormalY=0 NormalZ=1 AngleXU=0 Radius=2.5
  constraints (6):
    c: Coincident(g0,g-1)
    c: Diameter(g1) = 5
    c: Coincident(g1,g0)
    c: PointOnObject(g2,g-1)
    c: Equal(g2,g1)
    c: DistanceX(g2,g1) = 32.6
FEATURE [PartDesign::Pad] Pad
  Direction = (0,0,1)
  Length = 7
  Length2 = 10
  Profile = -> Sketch
  ReferenceAxis = -> Sketch [N_Axis]
  Type = 0
FEATURE [PartDesign::CoordinateSystem] LCS_idler1
  AttacherType = Attacher::AttachEngine3D
  AttachmentOffset = pos=(16.3,-7.5,7) rot=(0,0,1;0rad)
  MapMode = 2
  Placement = pos=(16.3,-7.5,7) rot=(0,0,1;0rad)
  Support = -> [XY_Plane001]
  expr: .AttachmentOffset.Base.x = Variables.IdlerMountOffsetX
  expr: .AttachmentOffset.Base.y = <<Variables>>.IdlerMountOffsetY * -1
  expr: .AttachmentOffset.Base.z = <<Pad>>.Length
FEATURE [PartDesign::CoordinateSystem] LCS_idler2
  AttacherType = Attacher::AttachEngine3D
  AttachmentOffset = pos=(-16.3,-7.5,7) rot=(0,0,1;0rad)
  MapMode = 2
  Placement = pos=(-16.3,-7.5,7) rot=(0,0,1;0rad)
  Support = -> [XY_Plane001]
  expr: .AttachmentOffset.Base.x = <<Variables>>.IdlerMountOffsetX * -1
  expr: .AttachmentOffset.Base.y = <<Variables>>.IdlerMountOffsetY * -1
  expr: .AttachmentOffset.Base.z = <<Pad>>.Length
FEATURE [Part::FeaturePython] Screw  label="M3x12-Screw"  # Fasteners workbench fastener (typed FeaturePython)
  Placement = pos=(-15.5,15.5,6) rot=(0,0,1;0rad)
  baseObject = -> Sketch003 [Edge1]
  diameter = 3
  invert = false
  leftHanded = false
  length = 2
  lengthCustom = 12
  matchOuter = true
  offset = 0
  thread = false
  type = 18
FEATURE [Part::FeaturePython] Screw001  label="M3x12-Screw094"  # Fasteners workbench fastener (typed FeaturePython)
  Placement = pos=(15.5,15.5,6) rot=(0,0,1;0rad)
  baseObject = -> Sketch003 [Edge2]
  diameter = 3
  invert = false
  leftHanded = false
  length = 2
  lengthCustom = 12
  matchOuter = true
  offset = 0
  thread = false
  type = 18
FEATURE [Part::FeaturePython] Screw002  label="M3x12-Screw095"  # Fasteners workbench fastener (typed FeaturePython)
  Placement = pos=(-15.5,-15.5,6) rot=(0,0,1;0rad)
  baseObject = -> Sketch003 [Edge4]
  diameter = 3
  invert = false
  leftHanded = false
  length = 2
  lengthCustom = 12
  matchOuter = true
  offset = 0
  thread = false
  type = 18
FEATURE [Part::FeaturePython] Screw003  label="M3x12-Screw096"  # Fasteners workbench fastener (typed FeaturePython)
  Placement = pos=(15.5,-15.5,6) rot=(0,0,1;0rad)
  baseObject = -> Sketch003 [Edge3]
  diameter = 3
  invert = false
  leftHanded = false
  length = 2
  lengthCustom = 12
  matchOuter = true
  offset = 0
  thread = false
  type = 18
FEATURE [Sketcher::SketchObject] Sketch003
  AttachmentOffset = pos=(0,0,6) rot=(0,0,1;0rad)
  FullyConstrained = true
  MapMode = 5
  Placement = pos=(0,0,6) rot=(0,0,1;0rad)
  Support = -> [XY_Plane001]
  expr: .AttachmentOffset.Base.z = <<Pad>>.Length - 1mm
  sketch-geometry (19):
    g0: LineSegment StartX=-15.5 StartY=15.5 StartZ=0 EndX=-15.5 EndY=-15.5 EndZ=0
    g1: LineSegment StartX=-15.5 StartY=-15.5 StartZ=0 EndX=15.5 EndY=-15.5 EndZ=0
    g2: LineSegment StartX=15.5 StartY=-15.5 StartZ=0 EndX=15.5 EndY=15.5 EndZ=0
    g3: LineSegment StartX=15.5 StartY=15.5 StartZ=0 EndX=-15.5 EndY=15.5 EndZ=0
    g4: GeomPoint X=0 Y=0 Z=0
    g5: Circle CenterX=-15.5 CenterY=15.5 CenterZ=0 NormalX=0 NormalY=0 NormalZ=1 AngleXU=0 Radius=1.7
    g6: Circle CenterX=15.5 CenterY=15.5 CenterZ=0 NormalX=0 NormalY=0 NormalZ=1 AngleXU=0 Radius=1.7
    g7: Circle CenterX=15.5 CenterY=-15.5 CenterZ=0 NormalX=0 NormalY=0 NormalZ=1 AngleXU=0 Radius=1.7
    g8: Circle CenterX=-15.5 CenterY=-15.5 CenterZ=0 NormalX=0 NormalY=0 NormalZ=1 AngleXU=0 Radius=1.7
    g9: ArcOfCircle CenterX=-15.5 CenterY=15.5 CenterZ=0 NormalX=0 NormalY=0 NormalZ=1 AngleXU=0 Radius=6 StartAngle=1.5708 EndAngle=3.14159
    g10: LineSegment StartX=-15.5 StartY=21.5 StartZ=0 EndX=15.5 EndY=21.5 EndZ=0
    g11: ArcOfCircle CenterX=15.5 CenterY=15.5 CenterZ=0 NormalX=0 NormalY=0 NormalZ=1 AngleXU=0 Radius=6 StartAngle=1e-16 EndAngle=1.5708
    g12: LineSegment StartX=21.5 StartY=15.5 StartZ=0 EndX=21.5 EndY=-13.5 EndZ=0
    g13: ArcOfCircle CenterX=15.5 CenterY=-13.5 CenterZ=0 NormalX=0 NormalY=0 NormalZ=1 AngleXU=0 Radius=6 StartAngle=4.71239 EndAngle=6.28319
    g14: LineSegment StartX=15.5 StartY=-19.5 StartZ=0 EndX=-15.5 EndY=-19.5 EndZ=0
    g15: ArcOfCircle CenterX=-15.5 CenterY=-13.5 CenterZ=0 NormalX=0 NormalY=0 NormalZ=1 AngleXU=0 Radius=6 StartAngle=3.14159 EndAngle=4.71239
    g16: LineSegment StartX=-21.5 StartY=-13.5 StartZ=0 EndX=-21.5 EndY=15.5 EndZ=0
    g17: GeomPoint X=-21.5 Y=21.5 Z=0
    g18: GeomPoint X=21.5 Y=-19.5 Z=0
  constraints (43):
    c: Coincident(g0,g1)
    c: Coincident(g1,g2)
    c: Coincident(g2,g3)
    c: Coincident(g3,g0)
    c: Horizontal(g1)
    c: Horizontal(g3)
    c: Vertical(g0)
    c: Vertical(g2)
    c: Symmetric(g1,g0,g4)
    c: Coincident(g4,g-1)
    c: Coincident(g5,g0)
    c: Coincident(g6,g2)
    c: Coincident(g7,g1)
    c: Coincident(g8,g0)
    c: Equal(g3,g0)
    c: Equal(g6,g5)
    c: Equal(g5,g8)
    c: Equal(g8,g7)
    c: Diameter(g6) = 3.4
    c: DistanceX(g3,g3) = 31
    c: Tangent(g9,g10) = 1.5708
    c: Tangent(g10,g11) = 1.5708
    c: Tangent(g11,g12) = 1.5708
    c: Tangent(g12,g13) = 1.5708
    c: Tangent(g13,g14) = 1.5708
    c: Tangent(g14,g15) = 1.5708
    c: Tangent(g15,g16) = 1.5708
    c: Tangent(g16,g9) = 1.5708
    c: Horizontal(g10)
    c: Horizontal(g14)
    c: Vertical(g12)
    c: Vertical(g16)
    c: Equal(g9,g11)
    c: Equal(g11,g13)
    c: Equal(g13,g15)
    c: PointOnObject(g17,g10)
    c: PointOnObject(g17,g16)
    c: PointOnObject(g18,g12)
    c: PointOnObject(g18,g14)
    c: Coincident(g9,g5)
    c: DistanceX(g9,g11) = 43
    c: PointOnObject(g13,g2)
    c: DistanceY(g13,g7) = 4
FEATURE [PartDesign::Hole] Hole001  label="IdlerHoleCountersink"
  BaseFeature = -> Pad
  CustomThreadClearance = 0
  Depth = 25
  DepthType = 0
  Diameter = 5.3
  DrillForDepth = false
  DrillPoint = 1
  DrillPointAngle = 118
  HoleCutCountersinkAngle = 90
  HoleCutCustomValues = false
  HoleCutDepth = 0
  HoleCutDiameter = 12.2
  HoleCutType = 7
  ModelThread = false
  Profile = -> Sketch001
  Reversed = true
  Tapered = false
  TaperedAngle = 90
  ThreadClass = 0
  ThreadDepth = 25
  ThreadDepthType = 0
  ThreadDirection = 0
  ThreadFit = 1
  ThreadSize = 13
  ThreadType = 1
  Threaded = false
  UseCustomThreadClearance = false
FEATURE [Part::FeaturePython] Screw004  label="M5x22-Screw"  # Fasteners workbench fastener (typed FeaturePython)
  Placement = pos=(16.3,-7.5,0.5) rot=(1,0,0;3.14159rad)
  baseObject = -> Sketch001 [Edge1]
  diameter = 5
  invert = true
  leftHanded = false
  length = 11
  lengthCustom = 22
  matchOuter = false
  offset = 0
  thread = false
  type = 18
FEATURE [Part::FeaturePython] Screw005  label="M5x22-Screw001"  # Fasteners workbench fastener (typed FeaturePython)
  Placement = pos=(-16.3,-7.5,0.5) rot=(1,0,0;3.14159rad)
  baseObject = -> Sketch001 [Edge2]
  diameter = 5
  invert = true
  leftHanded = false
  length = 11
  lengthCustom = 22
  matchOuter = false
  offset = 0
  thread = false
  type = 18
FEATURE [Part::FeaturePython] Nut  label="M5-Nut"  # Fasteners workbench fastener (typed FeaturePython)
  Placement = pos=(16.3,-7.5,17.5093) rot=(0,0,1;0rad)
  baseObject = -> Screw004 [Edge9]
  diameter = 3
  invert = true
  leftHanded = false
  matchOuter = false
  offset = -4.5
  thread = false
  type = 5
FEATURE [Part::FeaturePython] Nut001  label="M5-Nut001"  # Fasteners workbench fastener (typed FeaturePython)
  Placement = pos=(-16.3,-7.5,17.5093) rot=(0,0,1;0rad)
  baseObject = -> Screw005 [Edge9]
  diameter = 3
  invert = true
  leftHanded = false
  matchOuter = true
  offset = -4.5
  thread = false
  type = 5
FEATURE [App::DocumentObjectGroup] Fasteners
  Group = -> [Screw,Screw001,Screw002,Screw003,Screw004,Screw005,Nut,Nut001]
FEATURE [PartDesign::Hole] Hole002  label="IdlerHoleCounterBore"
  BaseFeature = -> Hole001
  CustomThreadClearance = 0
  Depth = 125.273
  DepthType = 1
  Diameter = 12.2
  DrillForDepth = false
  DrillPoint = 1
  DrillPointAngle = 118
  HoleCutCountersinkAngle = 90
  HoleCutCustomValues = false
  HoleCutDepth = 0
  HoleCutDiameter = 6.1
  HoleCutType = 0
  ModelThread = false
  Profile = -> Sketch001
  Tapered = false
  TaperedAngle = 90
  ThreadClass = 0
  ThreadDepth = 125.273
  ThreadDepthType = 0
  ThreadDirection = 0
  ThreadFit = 0
  ThreadSize = 0
  ThreadType = 0
  Threaded = false
  UseCustomThreadClearance = false
  expr: Diameter = <<IdlerHoleCountersink>>.HoleCutDiameter
FEATURE [PartDesign::Hole] Hole  label="StepperHoles"
  BaseFeature = -> Hole002
  CustomThreadClearance = 0
  Depth = 25
  DepthType = 0
  Diameter = 3.4
  DrillForDepth = false
  DrillPoint = 1
  DrillPointAngle = 118
  HoleCutCountersinkAngle = 90
  HoleCutCustomValues = false
  HoleCutDepth = 0
  HoleCutDiameter = 6.7
  HoleCutType = 7
  ModelThread = false
  Profile = -> Sketch003
  Tapered = false
  TaperedAngle = 90
  ThreadClass = 0
  ThreadDepth = 25
  ThreadDepthType = 0
  ThreadDirection = 0
  ThreadFit = 0
  ThreadSize = 9
  ThreadType = 1
  Threaded = false
  UseCustomThreadClearance = false
FEATURE [PartDesign::Hole] Hole003
  BaseFeature = -> Hole
  CustomThreadClearance = 0
  Depth = 125.273
  DepthType = 1
  Diameter = 6.7
  DrillForDepth = false
  DrillPoint = 1
  DrillPointAngle = 118
  HoleCutCountersinkAngle = 90
  HoleCutCustomValues = false
  HoleCutDepth = 0
  HoleCutDiameter = 6.1
  HoleCutType = 0
  ModelThread = false
  Profile = -> Sketch003
  Reversed = true
  Tapered = false
  TaperedAngle = 90
  ThreadClass = 0
  ThreadDepth = 125.273
  ThreadDepthType = 0
  ThreadDirection = 0
  ThreadFit = 0
  ThreadSize = 0
  ThreadType = 0
  Threaded = false
  UseCustomThreadClearance = false
  expr: Diameter = <<StepperHoles>>.HoleCutDiameter
FEATURE [PartDesign::Body] Body
  Group = -> [Sketch,Sketch001,Pad,Sketch003,Hole001,Hole002,Hole,Hole003]
  Origin = -> Origin001
  Tip = -> Hole003
FEATURE [App::Part] Assembly
  AssemblyType = Part::Link
  Group = -> [LCS_Origin,Variables,Constraints,Configurations,Body,LCS_idler1,LCS_idler2,Fasteners,Screw,Screw001,Screw002,Screw003,Screw004,Screw005,Nut,Nut001]
  Origin = -> Origin
  Type = Assembly
---- part SmoothIdlerPulleyGT2.FCStd = doc fcstd_959ed8b74e3e ----
FCSTD DOCUMENT  (FreeCAD 0.20R29177 +426 (Git))
Label: SmoothIdlerPulleyGT2
License: All rights reserved
LicenseURL: http://en.wikipedia.org/wiki/All_rights_reserved
objects: App::DocumentObjectGroup×3, PartDesign::CoordinateSystem×1, App::FeaturePython×1, Sketcher::SketchObject×1, PartDesign::Revolution×1, PartDesign::Body×1, App::Part×1
note: 5 computed .brp shape members not serialized (recipe doc carries the construction recipe); baked Part::Feature solids carry a one-line shape summary decoded from their .brp

FEATURE [App::DocumentObjectGroup] Parts
FEATURE [PartDesign::CoordinateSystem] LCS_Origin
  AttacherType = Attacher::AttachEngine3D
  MapMode = 2
  Support = -> [X_Axis]
FEATURE [App::FeaturePython] Variables  # WARN: FeaturePython — macro-defined, semantics opaque (R4)
  Type = App::PropertyContainer
FEATURE [App::DocumentObjectGroup] Constraints
FEATURE [App::DocumentObjectGroup] Configurations
FEATURE [Sketcher::SketchObject] Sketch
  FullyConstrained = true
  MapMode = 5
  Placement = pos=(0,0,0) rot=(1,0,0;1.5708rad)
  Support = -> [XZ_Plane001]
  sketch-geometry (8):
    g0: LineSegment StartX=2.51 StartY=0 StartZ=0 EndX=2.51 EndY=8.56 EndZ=0
    g1: LineSegment StartX=2.51 StartY=8.56 StartZ=0 EndX=9 EndY=8.56 EndZ=0
    g2: LineSegment StartX=9 StartY=8.56 StartZ=0 EndX=9 EndY=7.58 EndZ=0
    g3: LineSegment StartX=9 StartY=7.58 StartZ=0 EndX=6.045 EndY=7.58 EndZ=0
    g4: LineSegment StartX=6.045 StartY=7.58 StartZ=0 EndX=6.045 EndY=0.98 EndZ=0
    g5: LineSegment StartX=6.045 StartY=0.98 StartZ=0 EndX=9 EndY=0.98 EndZ=0
    g6: LineSegment StartX=9 StartY=0.98 StartZ=0 EndX=9 EndY=0 EndZ=0
    g7: LineSegment StartX=9 StartY=0 StartZ=0 EndX=2.51 EndY=0 EndZ=0
  constraints (24):
    c: PointOnObject(g0,g-1)
    c: Vertical(g0)
    c: Coincident(g0,g1)
    c: Horizontal(g1)
    c: Coincident(g1,g2)
    c: Coincident(g2,g3)
    c: Horizontal(g3)
    c: Coincident(g3,g4)
    c: Vertical(g4)
    c: Coincident(g4,g5)
    c: Horizontal(g5)
    c: Coincident(g5,g6)
    c: PointOnObject(g6,g-1)
    c: Vertical(g6)
    c: Coincident(g6,g7)
    c: Coincident(g7,g0)
    c: Vertical(g2)
    c: DistanceX(g-1,g3) = 6.045
    c: DistanceX(g-1,g0) = 2.51
    c: DistanceY(g4,g4) = 6.6
    c: PointOnObject(g2,g6)
    c: DistanceX(g-1,g6) = 9
    c: DistanceY(g-1,g0) = 8.56
    c: Equal(g2,g6)
FEATURE [PartDesign::Revolution] Revolution
  Angle = 360
  Axis = (0,-2e-16,1)
  Base = (0,0,0)
  Placement = pos=(0,0,0) rot=(1,0,0;1.5708rad)
  Profile = -> Sketch
  ReferenceAxis = -> Sketch [V_Axis]
  Reversed = true
FEATURE [PartDesign::Body] Body
  Group = -> [Sketch,Revolution]
  Origin = -> Origin001
  Tip = -> Revolution
FEATURE [App::Part] Assembly
  AssemblyType = Part::Link
  Group = -> [LCS_Origin,Variables,Constraints,Configurations,Body]
  Origin = -> Origin
  Type = Assembly
---- part Stepper17.FCStd = doc fcstd_2ae94f6e5666 ----
FCSTD DOCUMENT  (FreeCAD 0.20R29177 +426 (Git))
Label: Stepper17
License: All rights reserved
LicenseURL: http://en.wikipedia.org/wiki/All_rights_reserved
objects: Sketcher::SketchObject×5, PartDesign::Pad×3, PartDesign::Pocket×2, PartDesign::Chamfer×1, PartDesign::PolarPattern×1, PartDesign::CoordinateSystem×1, PartDesign::Body×1
note: 20 computed .brp shape members not serialized (recipe doc carries the construction recipe); baked Part::Feature solids carry a one-line shape summary decoded from their .brp

FEATURE [Sketcher::SketchObject] Sketch
  FullyConstrained = true
  MapMode = 5
  Support = -> [XY_Plane]
  sketch-geometry (4):
    g0: LineSegment StartX=-21 StartY=21 StartZ=0 EndX=21 EndY=21 EndZ=0
    g1: LineSegment StartX=21 StartY=21 StartZ=0 EndX=21 EndY=-21 EndZ=0
    g2: LineSegment StartX=21 StartY=-21 StartZ=0 EndX=-21 EndY=-21 EndZ=0
    g3: LineSegment StartX=-21 StartY=-21 StartZ=0 EndX=-21 EndY=21 EndZ=0
  constraints (11):
    c: Coincident(g0,g1)
    c: Coincident(g1,g2)
    c: Coincident(g2,g3)
    c: Coincident(g3,g0)
    c: Horizontal(g0)
    c: Horizontal(g2)
    c: Vertical(g1)
    c: Vertical(g3)
    c: Symmetric(g0,g2,g-1)
    c: Equal(g1,g0)
    c: DistanceX(g0,g0) = 42
FEATURE [PartDesign::Pad] Pad
  Direction = (1,1,1)
  Length = 48
  Length2 = 100
  Profile = -> Sketch
  Type = 0
FEATURE [PartDesign::Chamfer] Chamfer
  Angle = 45
  Base = -> Pad [Edge5,Edge8,Edge2,Edge1]
  BaseFeature = -> Pad
  ChamferType = 0
  FlipDirection = false
  Size = 4
  Size2 = 1
  SupportTransform = false
  UseAllEdges = false
FEATURE [Sketcher::SketchObject] Sketch001
  FullyConstrained = true
  MapMode = 5
  Support = -> [XY_Plane]
  sketch-geometry (1):
    g0: Circle CenterX=0 CenterY=0 CenterZ=0 NormalX=0 NormalY=0 NormalZ=1 AngleXU=0 Radius=11
  constraints (2):
    c: Coincident(g0,g-1)
    c: Diameter(g0) = 22
FEATURE [PartDesign::Pad] Pad001
  BaseFeature = -> Chamfer
  Direction = (1,1,1)
  Length = 2
  Length2 = 100
  Profile = -> Sketch001
  Reversed = true
  Type = 0
FEATURE [Sketcher::SketchObject] Sketch002
  FullyConstrained = true
  MapMode = 5
  Placement = pos=(0,0,-2) rot=(1,0,0;3.14159rad)
  Support = -> [Pad001]
  sketch-geometry (1):
    g0: Circle CenterX=0 CenterY=0 CenterZ=0 NormalX=0 NormalY=0 NormalZ=1 AngleXU=0 Radius=2.5
  constraints (2):
    c: Coincident(g0,g-1)
    c: Diameter(g0) = 5
FEATURE [PartDesign::Pad] Pad002
  BaseFeature = -> Pad001
  Direction = (1,1,1)
  Length = 24
  Length2 = 100
  Profile = -> Sketch002
  Type = 0
FEATURE [Sketcher::SketchObject] Sketch003
  ExternalGeometry = -> [Pad002]
  FullyConstrained = true
  MapMode = 5
  Placement = pos=(0,0,-26) rot=(1,0,0;3.14159rad)
  Support = -> [Pad002]
  sketch-geometry (2):
    g0: ArcOfCircle CenterX=0 CenterY=0 CenterZ=0 NormalX=0 NormalY=0 NormalZ=1 AngleXU=0 Radius=2.5 StartAngle=0.927295 EndAngle=2.2143
    g1: LineSegment StartX=-1.5 StartY=2 StartZ=0 EndX=1.5 EndY=2 EndZ=0
  constraints (6):
    c: Coincident(g0,g-1)
    c: PointOnObject(g0,g-3)
    c: Coincident(g1,g0)
    c: Coincident(g1,g0)
    c: DistanceY(g0,g0) = 2
    c: Horizontal(g1)
FEATURE [PartDesign::Pocket] Pocket
  BaseFeature = -> Pad002
  Direction = (1,1,1)
  Length = 15
  Length2 = 100
  Profile = -> Sketch003
  Type = 0
FEATURE [Sketcher::SketchObject] Sketch004
  FullyConstrained = true
  MapMode = 5
  Placement = pos=(0,0,0) rot=(1,0,0;3.14159rad)
  Support = -> [Pocket]
  sketch-geometry (4):
    g0: LineSegment StartX=0 StartY=0 StartZ=0 EndX=0 EndY=15.5 EndZ=0
    g1: LineSegment StartX=0 StartY=15.5 StartZ=0 EndX=15.5 EndY=15.5 EndZ=0
    g2: LineSegment StartX=15.5 StartY=15.5 StartZ=0 EndX=0 EndY=0 EndZ=0
    g3: Circle CenterX=15.5 CenterY=15.5 CenterZ=0 NormalX=0 NormalY=0 NormalZ=1 AngleXU=0 Radius=1.25
  constraints (10):
    c: Coincident(g0,g-1)
    c: PointOnObject(g0,g-2)
    c: Coincident(g1,g0)
    c: Horizontal(g1)
    c: Coincident(g2,g1)
    c: Coincident(g2,g-1)
    c: Equal(g0,g1)
    c: DistanceX(g1,g1) = 15.5
    c: Coincident(g3,g1)
    c: Diameter(g3) = 2.5
FEATURE [PartDesign::Pocket] Pocket001
  BaseFeature = -> Pocket
  Direction = (1,1,1)
  Length = 5
  Length2 = 100
  Profile = -> Sketch004
  Type = 0
FEATURE [PartDesign::PolarPattern] PolarPattern
  Angle = 360
  Axis = -> Z_Axis
  BaseFeature = -> Pocket001
  Occurrences = 4
  Originals = -> [Pocket001]
FEATURE [PartDesign::CoordinateSystem] LCS_mount
  AttacherType = Attacher::AttachEngine3D
  MapMode = 2
  Support = -> [XY_Plane]
FEATURE [PartDesign::Body] Body
  Group = -> [Sketch,Pad,Chamfer,Sketch001,Pad001,Sketch002,Pad002,Sketch003,Pocket,Sketch004,Pocket001,PolarPattern,LCS_mount]
  Origin = -> Origin
  Tip = -> PolarPattern
---- part Stepper17BracketFlat.FCStd = doc fcstd_b93b1507b154 ----
FCSTD DOCUMENT  (FreeCAD 0.20R29177 +426 (Git))
Label: Stepper17BracketFlat
License: All rights reserved
LicenseURL: http://en.wikipedia.org/wiki/All_rights_reserved
objects: App::DocumentObjectGroup×3, PartDesign::CoordinateSystem×2, Sketcher::SketchObject×2, App::FeaturePython×1, PartDesign::Pad×1, PartDesign::Hole×1, PartDesign::Body×1, App::Part×1
note: 9 computed .brp shape members not serialized (recipe doc carries the construction recipe); baked Part::Feature solids carry a one-line shape summary decoded from their .brp

FEATURE [App::DocumentObjectGroup] Parts
FEATURE [PartDesign::CoordinateSystem] LCS_Origin
  AttacherType = Attacher::AttachEngine3D
  MapMode = 2
  Support = -> [X_Axis]
FEATURE [App::FeaturePython] Variables  # WARN: FeaturePython — macro-defined, semantics opaque (R4)
  Type = App::PropertyContainer
FEATURE [App::DocumentObjectGroup] Constraints
FEATURE [App::DocumentObjectGroup] Configurations
FEATURE [Sketcher::SketchObject] Sketch
  FullyConstrained = true
  MapMode = 5
  Support = -> [XY_Plane001]
  sketch-geometry (38):
    g0: Circle CenterX=0 CenterY=0 CenterZ=0 NormalX=0 NormalY=0 NormalZ=1 AngleXU=0 Radius=11.25
    g1: GeomPoint X=0 Y=-29 Z=0
    g2: ArcOfCircle CenterX=-15 CenterY=-39 CenterZ=0 NormalX=0 NormalY=0 NormalZ=1 AngleXU=0 Radius=2.15 StartAngle=0 EndAngle=3.14159
    g3: ArcOfCircle CenterX=-15 CenterY=-68.5 CenterZ=0 NormalX=0 NormalY=0 NormalZ=1 AngleXU=0 Radius=2.15 StartAngle=3.14159 EndAngle=6.28319
    g4: LineSegment StartX=-17.15 StartY=-39 StartZ=0 EndX=-17.15 EndY=-68.5 EndZ=0
    g5: LineSegment StartX=-12.85 StartY=-68.5 StartZ=0 EndX=-12.85 EndY=-39 EndZ=0
    g6: GeomPoint X=-15 Y=-36.85 Z=0
    g7: GeomPoint X=-15 Y=-70.65 Z=0
    g8: LineSegment StartX=-15 StartY=-36.85 StartZ=0 EndX=-15 EndY=-70.65 EndZ=0
    g9: ArcOfCircle CenterX=15 CenterY=-39 CenterZ=0 NormalX=0 NormalY=0 NormalZ=1 AngleXU=0 Radius=2.15 StartAngle=3.062e-13 EndAngle=3.14159
    g10: ArcOfCircle CenterX=15 CenterY=-68.5 CenterZ=0 NormalX=0 NormalY=0 NormalZ=1 AngleXU=0 Radius=2.15 StartAngle=3.14159 EndAngle=6.28319
    g11: LineSegment StartX=12.85 StartY=-39 StartZ=0 EndX=12.85 EndY=-68.5 EndZ=0
    g12: LineSegment StartX=17.15 StartY=-68.5 StartZ=0 EndX=17.15 EndY=-39 EndZ=0
    g13: GeomPoint X=15 Y=-36.85 Z=0
    g14: GeomPoint X=15 Y=-70.65 Z=0
    g15: LineSegment StartX=15 StartY=-36.85 StartZ=0 EndX=15 EndY=-70.65 EndZ=0
    g16: LineSegment StartX=-15 StartY=-39 StartZ=0 EndX=0 EndY=-39 EndZ=0
    g17: LineSegment StartX=0 StartY=-39 StartZ=0 EndX=15 EndY=-39 EndZ=0
    g18: LineSegment StartX=0 StartY=0 StartZ=0 EndX=15.5 EndY=15.5 EndZ=0
    g19: LineSegment StartX=15.5 StartY=15.5 StartZ=0 EndX=15.5 EndY=0 EndZ=0
    g20: Circle CenterX=15.5 CenterY=15.5 CenterZ=0 NormalX=0 NormalY=0 NormalZ=1 AngleXU=0 Radius=1.75
    g21: LineSegment StartX=25 StartY=21 StartZ=0 EndX=20.5 EndY=21 EndZ=0
    g22: LineSegment StartX=25 StartY=16.5 StartZ=0 EndX=25 EndY=21 EndZ=0
    g23: LineSegment StartX=-25 StartY=21 StartZ=0 EndX=-25 EndY=16.5 EndZ=0
    g24: LineSegment StartX=20.5 StartY=21 StartZ=0 EndX=-20.5 EndY=21 EndZ=0
    g25: LineSegment StartX=-20.5 StartY=21 StartZ=0 EndX=-25 EndY=21 EndZ=0
    g26: LineSegment StartX=-25 StartY=-79 StartZ=0 EndX=-20.5 EndY=-79 EndZ=0
    g27: LineSegment StartX=-25 StartY=16.5 StartZ=0 EndX=-25 EndY=-74.5 EndZ=0
    g28: LineSegment StartX=-25 StartY=-74.5 StartZ=0 EndX=-25 EndY=-79 EndZ=0
    g29: LineSegment StartX=-20.5 StartY=-79 StartZ=0 EndX=20.5 EndY=-79 EndZ=0
    g30: LineSegment StartX=20.5 StartY=-79 StartZ=0 EndX=25 EndY=-79 EndZ=0
    g31: LineSegment StartX=25 StartY=-79 StartZ=0 EndX=25 EndY=-74.5 EndZ=0
    g32: LineSegment StartX=25 StartY=-74.5 StartZ=0 EndX=25 EndY=16.5 EndZ=0
    g33: LineSegment StartX=-20.5 StartY=-79 StartZ=0 EndX=-25 EndY=-74.5 EndZ=0
    g34: LineSegment StartX=25 StartY=-74.5 StartZ=0 EndX=20.5 EndY=-79 EndZ=0
    g35: LineSegment StartX=25 StartY=16.5 StartZ=0 EndX=20.5 EndY=21 EndZ=0
    g36: LineSegment StartX=-25 StartY=16.5 StartZ=0 EndX=-20.5 EndY=21 EndZ=0
    g37: Circle CenterX=4.1e-15 CenterY=-53.75 CenterZ=0 NormalX=0 NormalY=0 NormalZ=1 AngleXU=0 Radius=5
  constraints (95):
    c: Coincident(g0,g-1)
    c: Diameter(g0) = 22.5
    c: Coincident(g22,g21)
    c: Coincident(g25,g23)
    c: Coincident(g28,g26)
    c: Coincident(g30,g31)
    c: Symmetric(g25,g31,g1)
    c: PointOnObject(g1,g-2)
    c: DistanceX(g25,g21) = 50
    c: DistanceY(g31,g22) = 100
    c: Tangent(g2,g4) = -1.5708
    c: Tangent(g4,g3) = -1.5708
    c: Tangent(g3,g5) = -1.5708
    c: Tangent(g5,g2) = -1.5708
    c: Equal(g2,g3)
    c: Vertical(g4)
    c: Diameter(g2) = 4.3
    c: PointOnObject(g6,g2)
    c: PointOnObject(g7,g3)
    c: Coincident(g8,g6)
    c: Coincident(g8,g7)
    c: Vertical(g8)
    c: PointOnObject(g3,g8)
    c: DistanceY(g8,g8) = 33.8
    c: Tangent(g9,g11) = -1.5708
    c: Tangent(g11,g10) = -1.5708
    c: Tangent(g10,g12) = -1.5708
    c: Tangent(g12,g9) = -1.5708
    c: Equal(g9,g10)
    c: Vertical(g11)
    c: Equal(g2,g9) = 4.3
    c: PointOnObject(g13,g9)
    c: PointOnObject(g14,g10)
    c: Coincident(g15,g13)
    c: Coincident(g15,g14)
    c: Vertical(g15)
    c: PointOnObject(g10,g15)
    c: Equal(g8,g15) = 33.8
    c: Coincident(g16,g2)
    c: PointOnObject(g16,g-2)
    c: Horizontal(g16)
    c: Coincident(g16,g17)
    c: Coincident(g17,g9)
    c: Horizontal(g17)
    c: Equal(g16,g17)
    c: DistanceX(g2,g9) = 30  'SlotSpacing'
    c: DistanceY(g28,g16) = 40
    c: Coincident(g18,g0)
    c: Angle(g-1,g18) = 0.785398
    c: Coincident(g19,g18)
    c: PointOnObject(g19,g-1)
    c: Vertical(g19)
    c: DistanceY(g19,g19) = 15.5
    c: Coincident(g20,g18)
    c: Diameter(g20) = 3.5
    c: DistanceY(g0,g25) = 21
    c: Coincident(g21,g24)
    c: Horizontal(g21)
    c: Coincident(g32,g22)
    c: Vertical(g22)
    c: Coincident(g23,g27)
    c: Vertical(g23)
    c: Coincident(g24,g25)
    c: Horizontal(g24)
    c: Horizontal(g25)
    c: Coincident(g26,g29)
    c: Horizontal(g26)
    c: Coincident(g27,g28)
    c: Vertical(g27)
    c: Vertical(g28)
    c: Coincident(g29,g30)
    c: Horizontal(g29)
    c: Horizontal(g30)
    c: Coincident(g31,g32)
    c: Vertical(g31)
    c: Vertical(g32)
    c: Equal(g31,g30)
    c: Equal(g30,g26)
    c: Equal(g26,g28)
    c: Equal(g28,g22)
    c: Equal(g22,g21)
    c: Equal(g21,g25)
    c: Equal(g25,g23)
    c: DistanceX(g25,g25) = 4.5
    c: Coincident(g33,g29)
    c: Coincident(g33,g27)
    c: Coincident(g34,g32)
    c: Coincident(g34,g29)
    c: Coincident(g35,g32)
    c: Coincident(g35,g24)
    c: Coincident(g36,g27)
    c: Coincident(g36,g24)
    c: Diameter(g37) = 10
    c: Symmetric(g3,g9,g37)
    c: DistanceY(g37,g0) = 53.75  'MountOffset'
FEATURE [PartDesign::Pad] Pad
  Direction = (0,0,1)
  Length = 3
  Length2 = 10
  Profile = -> Sketch
  ReferenceAxis = -> Sketch [N_Axis]
  Type = 0
FEATURE [Sketcher::SketchObject] Sketch001
  FullyConstrained = true
  MapMode = 5
  Support = -> [XY_Plane001]
  sketch-geometry (9):
    g0: LineSegment StartX=-15.5 StartY=-15.5 StartZ=0 EndX=-15.5 EndY=15.5 EndZ=0
    g1: LineSegment StartX=-15.5 StartY=15.5 StartZ=0 EndX=15.5 EndY=15.5 EndZ=0
    g2: LineSegment StartX=15.5 StartY=15.5 StartZ=0 EndX=15.5 EndY=-15.5 EndZ=0
    g3: LineSegment StartX=15.5 StartY=-15.5 StartZ=0 EndX=-15.5 EndY=-15.5 EndZ=0
    g4: GeomPoint X=0 Y=0 Z=0
    g5: Circle CenterX=-15.5 CenterY=15.5 CenterZ=0 NormalX=0 NormalY=0 NormalZ=1 AngleXU=0 Radius=1
    g6: Circle CenterX=15.5 CenterY=15.5 CenterZ=0 NormalX=0 NormalY=0 NormalZ=1 AngleXU=0 Radius=1
    g7: Circle CenterX=15.5 CenterY=-15.5 CenterZ=0 NormalX=0 NormalY=0 NormalZ=1 AngleXU=0 Radius=1
    g8: Circle CenterX=-15.5 CenterY=-15.5 CenterZ=0 NormalX=0 NormalY=0 NormalZ=1 AngleXU=0 Radius=1
  constraints (20):
    c: Coincident(g0,g1)
    c: Coincident(g1,g2)
    c: Coincident(g2,g3)
    c: Coincident(g3,g0)
    c: Horizontal(g1)
    c: Horizontal(g3)
    c: Vertical(g0)
    c: Vertical(g2)
    c: Symmetric(g1,g0,g4)
    c: Coincident(g4,g-1)
    c: DistanceY(g2,g2) = 31
    c: Equal(g2,g1)
    c: Coincident(g5,g0)
    c: Coincident(g6,g1)
    c: Coincident(g7,g2)
    c: Coincident(g8,g0)
    c: Equal(g8,g5)
    c: Equal(g5,g6)
    c: Equal(g6,g7)
    c: Diameter(g6) = 2
FEATURE [PartDesign::Hole] Hole
  BaseFeature = -> Pad
  CustomThreadClearance = 0
  Depth = 25
  DepthType = 0
  Diameter = 3.4
  DrillForDepth = false
  DrillPoint = 1
  DrillPointAngle = 118
  HoleCutCountersinkAngle = 90
  HoleCutCustomValues = false
  HoleCutDepth = 0
  HoleCutDiameter = 6.1
  HoleCutType = 0
  ModelThread = false
  Profile = -> Sketch001
  Reversed = true
  Tapered = false
  TaperedAngle = 90
  ThreadClass = 0
  ThreadDepth = 25
  ThreadDepthType = 0
  ThreadDirection = 0
  ThreadFit = 0
  ThreadSize = 9
  ThreadType = 1
  Threaded = false
  UseCustomThreadClearance = false
FEATURE [PartDesign::Body] Body
  Group = -> [Sketch,Pad,Sketch001,Hole]
  Origin = -> Origin001
  Tip = -> Hole
FEATURE [PartDesign::CoordinateSystem] LCS_Mount
  AttacherType = Attacher::AttachEngine3D
  AttachmentOffset = pos=(0,-53.75,0) rot=(0,0,1;0rad)
  MapMode = 2
  Placement = pos=(0,-53.75,0) rot=(0,0,1;0rad)
  Support = -> [LCS_Origin]
  expr: .AttachmentOffset.Base.y = <<Sketch>>.Constraints.MountOffset * -1
FEATURE [App::Part] Assembly
  AssemblyType = Part::Link
  Group = -> [LCS_Origin,Variables,Constraints,Configurations,Body,LCS_Mount]
  Origin = -> Origin
  Type = Assembly
---- part TimingPulleyGT2.FCStd = doc fcstd_5d79afefdc93 ----
FCSTD DOCUMENT  (FreeCAD 0.20R29177 +426 (Git))
Label: TimingPulleyGT2
License: All rights reserved
LicenseURL: http://en.wikipedia.org/wiki/All_rights_reserved
objects: App::DocumentObjectGroup×3, PartDesign::CoordinateSystem×1, App::FeaturePython×1, Sketcher::SketchObject×1, PartDesign::Revolution×1, PartDesign::Body×1, App::Part×1
note: 5 computed .brp shape members not serialized (recipe doc carries the construction recipe); baked Part::Feature solids carry a one-line shape summary decoded from their .brp

FEATURE [App::DocumentObjectGroup] Parts
FEATURE [PartDesign::CoordinateSystem] LCS_Origin
  AttacherType = Attacher::AttachEngine3D
  MapMode = 2
  Support = -> [X_Axis]
FEATURE [App::FeaturePython] Variables  # WARN: FeaturePython — macro-defined, semantics opaque (R4)
  Type = App::PropertyContainer
FEATURE [App::DocumentObjectGroup] Constraints
FEATURE [App::DocumentObjectGroup] Configurations
FEATURE [Sketcher::SketchObject] Sketch
  FullyConstrained = true
  MapMode = 5
  Placement = pos=(0,0,0) rot=(1,0,0;1.5708rad)
  Support = -> [XZ_Plane001]
  sketch-geometry (8):
    g0: LineSegment StartX=2.51 StartY=0 StartZ=0 EndX=2.51 EndY=16 EndZ=0
    g1: LineSegment StartX=2.51 StartY=16 StartZ=0 EndX=8 EndY=16 EndZ=0
    g2: LineSegment StartX=8 StartY=16 StartZ=0 EndX=8 EndY=14.1 EndZ=0
    g3: LineSegment StartX=8 StartY=14.1 StartZ=0 EndX=6.11 EndY=14.1 EndZ=0
    g4: LineSegment StartX=6.11 StartY=14.1 StartZ=0 EndX=6.11 EndY=7.1 EndZ=0
    g5: LineSegment StartX=6.11 StartY=7.1 StartZ=0 EndX=8 EndY=7.1 EndZ=0
    g6: LineSegment StartX=8 StartY=7.1 StartZ=0 EndX=8 EndY=0 EndZ=0
    g7: LineSegment StartX=8 StartY=0 StartZ=0 EndX=2.51 EndY=0 EndZ=0
  constraints (24):
    c: PointOnObject(g0,g-1)
    c: Vertical(g0)
    c: Coincident(g0,g1)
    c: Horizontal(g1)
    c: Coincident(g1,g2)
    c: Coincident(g2,g3)
    c: Horizontal(g3)
    c: Coincident(g3,g4)
    c: Vertical(g4)
    c: Coincident(g4,g5)
    c: Horizontal(g5)
    c: Coincident(g5,g6)
    c: PointOnObject(g6,g-1)
    c: Vertical(g6)
    c: Coincident(g6,g7)
    c: Coincident(g7,g0)
    c: Vertical(g2)
    c: DistanceX(g-1,g3) = 6.11
    c: DistanceX(g-1,g0) = 2.51
    c: DistanceY(g4,g4) = 7
    c: PointOnObject(g2,g6)
    c: DistanceY(g6,g6) = 7.1
    c: DistanceX(g-1,g6) = 8
    c: DistanceY(g-1,g0) = 16
FEATURE [PartDesign::Revolution] Revolution
  Angle = 360
  Axis = (0,2e-16,1)
  Base = (0,0,0)
  Placement = pos=(0,0,0) rot=(1,0,0;1.5708rad)
  Profile = -> Sketch
  ReferenceAxis = -> Sketch [V_Axis]
  Reversed = true
FEATURE [PartDesign::Body] Body
  Group = -> [Sketch,Revolution]
  Origin = -> Origin001
  Tip = -> Revolution
FEATURE [App::Part] Assembly
  AssemblyType = Part::Link
  Group = -> [LCS_Origin,Variables,Constraints,Configurations,Body]
  Origin = -> Origin
  Type = Assembly
